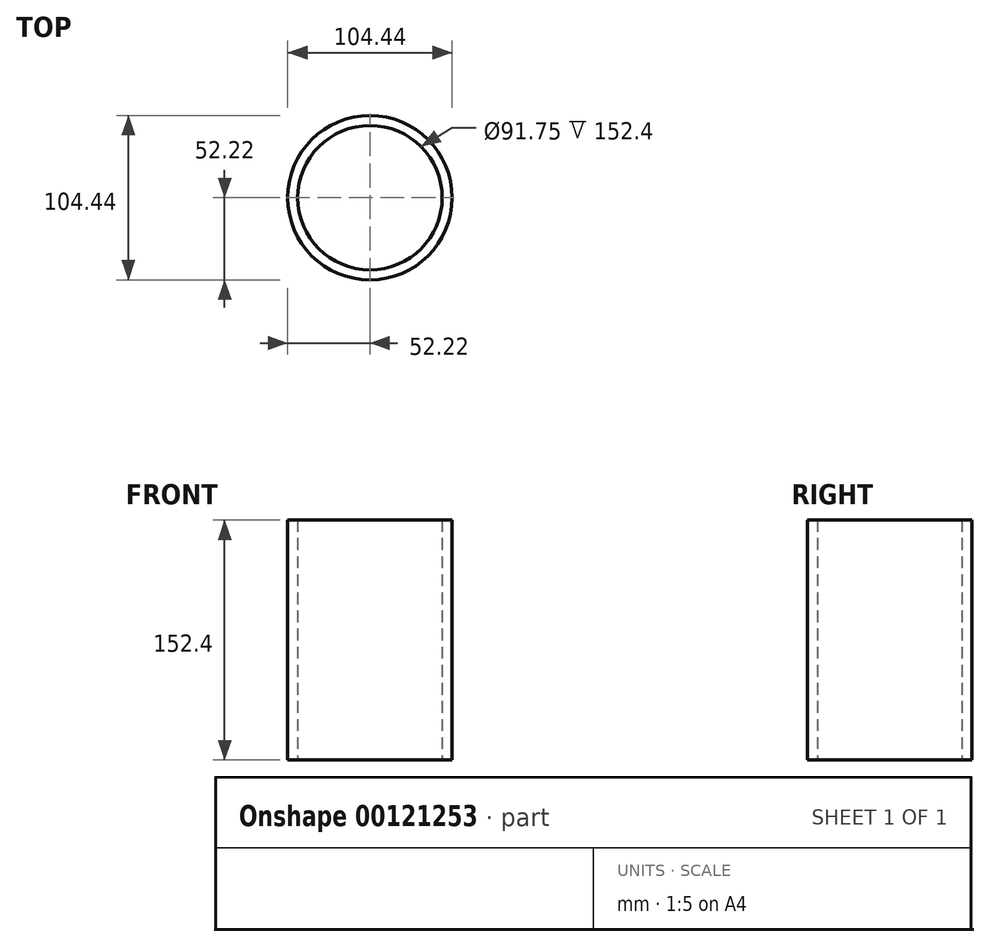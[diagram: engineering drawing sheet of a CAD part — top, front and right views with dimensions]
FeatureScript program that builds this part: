
annotation { "Feature Type Name" : "Feature", "Feature Type Description" : "" }
export const myFeature = defineFeature(function(context is Context, id is Id, definition is map)
    precondition{}
    {
        {
            var Q0;
            Q0=qCreatedBy(makeId("Top.planeOp"),FACE);
            var sketch = newSketch(context, id + "F0", { "sketchPlane" : qUnion([Q0])});
            skCircle(sketch, "E0", {"center": v(0, 0) * mm, "radius": 45.87 * mm});
            skCircle(sketch, "E1.0", {"center": v(0, 0) * mm, "radius": 52.22 * mm});
            skSolve(sketch);
        }
        {
            var Q0;
            Q0=makeQuery(id+"F0.imprint","IMPRINT",FACE,{"disambiguationData":[TD([[makeQuery(id+"F0.imprint","IMPRINT",EDGE,{"derivedFrom":sQuery(id+"F0.wireOp",EDGE,"E0")}),-1.0]])]});
            var Q1;
            Q1=sQuery(id+"F0.wireOp",EDGE,"E1.0");
            var Q2;
            Q2=sQuery(id+"F0.wireOp",EDGE,"E0");
            extrude(context, id + "F1", {"entities" : qUnion([Q0]), "surfaceEntities" : qUnion([Q1, Q2]), "depth" : 152.4 * mm});
        }
    });
